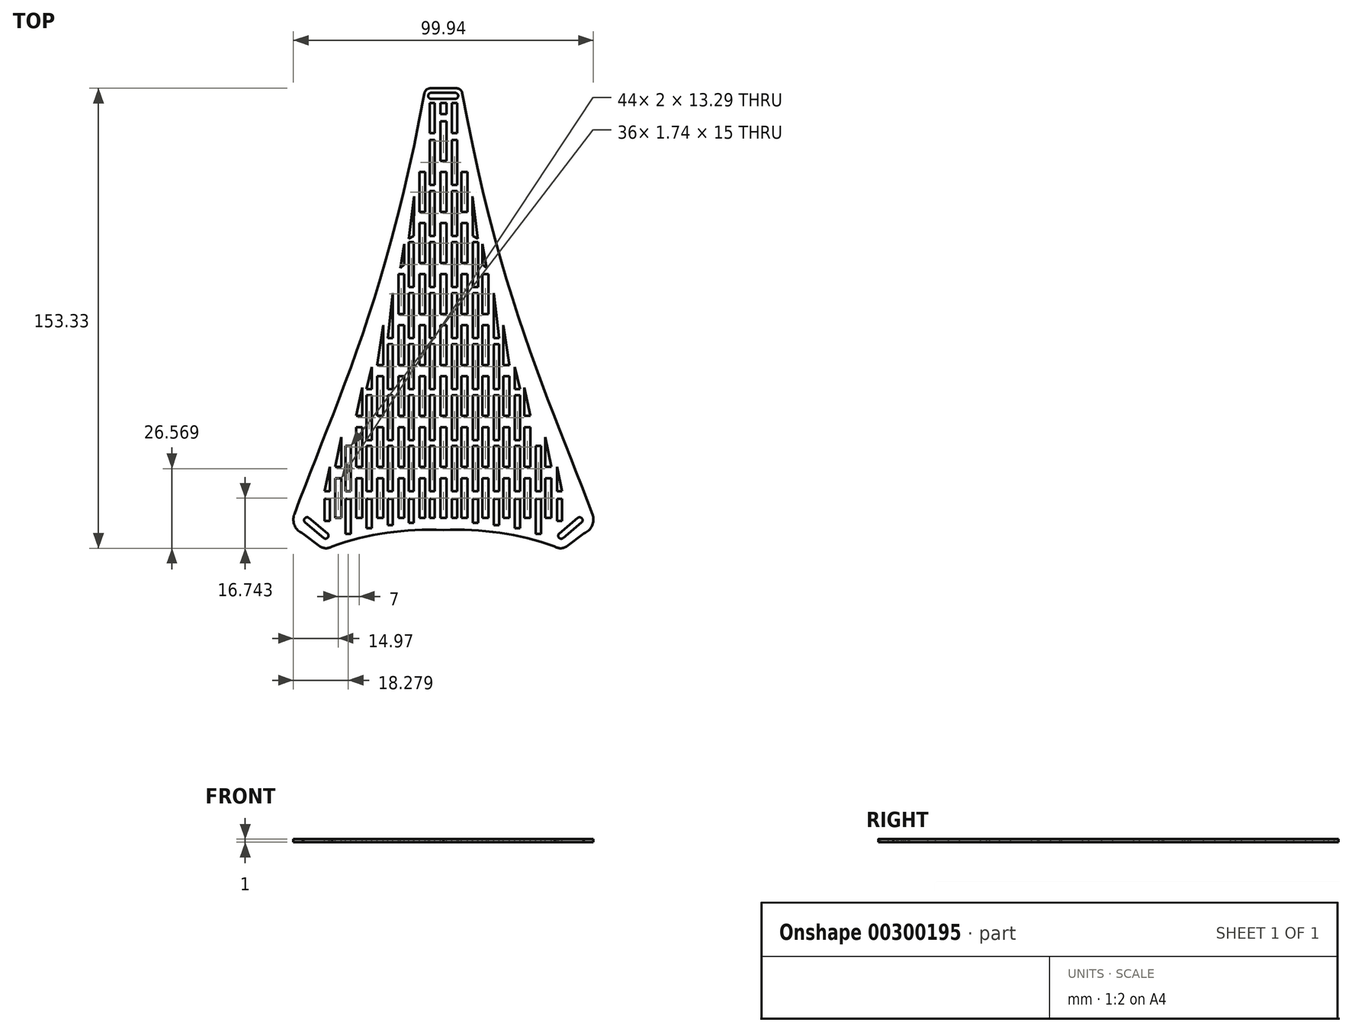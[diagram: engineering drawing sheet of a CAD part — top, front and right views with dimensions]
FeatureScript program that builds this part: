
annotation { "Feature Type Name" : "Feature", "Feature Type Description" : "" }
export const myFeature = defineFeature(function(context is Context, id is Id, definition is map)
    precondition{}
    {
        {
            var Q0;
            Q0=qCreatedBy(makeId("Top.planeOp"),FACE);
            var sketch = newSketch(context, id + "F0", { "sketchPlane" : qUnion([Q0])});
            skFitSpline(sketch, "E0", {"points": [v(-6, 109.23) * mm, v(-51.73, -38.5) * mm], "startDerivative": vector(-41.27, -226.26) * mm, "endDerivative": vector(-40.91, -115.5) * mm});
            skLineSegment(sketch, "E1", {"start": v(-4.34, 109.23) * mm, "end": v(0, 109.23) * mm});
            skArc(sketch, "E2.filletArc", {"start": v(-4.34, 109.23) * mm, "mid": v(-5.62, 108.76) * mm, "end": v(-6.3, 107.6) * mm});
            skArc(sketch, "E3.filletArc", {"start": v(-49.66, -32.79) * mm, "mid": v(-49.54, -36.57) * mm, "end": v(-46.8, -39.17) * mm});
            skLineSegment(sketch, "E4.bottom", {"start": v(-44.75, -34) * mm, "end": v(-38.62, -39.14) * mm});
            skLineSegment(sketch, "E4.top", {"start": v(-46.03, -35.53) * mm, "end": v(-39.9, -40.68) * mm});
            skLineSegment(sketch, "E4.left", {"start": v(-46.16, -34.13) * mm, "end": v(-46.16, -34.13) * mm});
            skLineSegment(sketch, "E4.right", {"start": v(-38.5, -40.55) * mm, "end": v(-38.5, -40.55) * mm});
            skPoint(sketch, "E5.visualSharp", {"position": v(-45.51, -33.36) * mm});
            skArc(sketch, "E5.filletArc", {"start": v(-44.75, -34) * mm, "mid": v(-45.48, -33.77) * mm, "end": v(-46.16, -34.13) * mm});
            skPoint(sketch, "E6.visualSharp", {"position": v(-46.8, -34.9) * mm});
            skArc(sketch, "E6.filletArc", {"start": v(-46.16, -34.13) * mm, "mid": v(-46.39, -34.86) * mm, "end": v(-46.03, -35.53) * mm});
            skPoint(sketch, "E7.visualSharp", {"position": v(-39.14, -41.32) * mm});
            skArc(sketch, "E7.filletArc", {"start": v(-39.9, -40.68) * mm, "mid": v(-39.17, -40.9) * mm, "end": v(-38.5, -40.55) * mm});
            skPoint(sketch, "E8.visualSharp", {"position": v(-37.85, -39.79) * mm});
            skArc(sketch, "E8.filletArc", {"start": v(-38.5, -40.55) * mm, "mid": v(-38.27, -39.82) * mm, "end": v(-38.62, -39.14) * mm});
            skLineSegment(sketch, "E9.bottom", {"start": v(-4.06, 107.72) * mm, "end": v(3.94, 107.72) * mm});
            skLineSegment(sketch, "E9.top", {"start": v(-4.06, 105.72) * mm, "end": v(3.94, 105.72) * mm});
            skLineSegment(sketch, "E9.left", {"start": v(-4.76, 104.67) * mm, "end": v(-4.76, 104.67) * mm});
            skLineSegment(sketch, "E9.right", {"start": v(5.24, 104.67) * mm, "end": v(5.24, 104.67) * mm});
            skPoint(sketch, "E10.visualSharp", {"position": v(-5.06, 107.18) * mm});
            skArc(sketch, "E10.filletArc", {"start": v(-4.06, 107.72) * mm, "mid": v(-4.77, 107.43) * mm, "end": v(-5.06, 106.72) * mm});
            skPoint(sketch, "E11.visualSharp", {"position": v(-5.06, 105.18) * mm});
            skArc(sketch, "E11.filletArc", {"start": v(-5.06, 106.72) * mm, "mid": v(-4.77, 106.01) * mm, "end": v(-4.06, 105.72) * mm});
            skPoint(sketch, "E12.visualSharp", {"position": v(4.94, 105.18) * mm});
            skArc(sketch, "E12.filletArc", {"start": v(3.94, 105.72) * mm, "mid": v(4.65, 106.01) * mm, "end": v(4.94, 106.72) * mm});
            skPoint(sketch, "E13.visualSharp", {"position": v(4.94, 107.18) * mm});
            skArc(sketch, "E13.filletArc", {"start": v(4.94, 106.72) * mm, "mid": v(4.65, 107.43) * mm, "end": v(3.94, 107.72) * mm});
            skArc(sketch, "E14.MirrorCS", {"start": v(46.16, -34.13) * mm, "mid": v(46.39, -34.86) * mm, "end": v(46.03, -35.53) * mm});
            skArc(sketch, "E15.MirrorCS", {"start": v(44.75, -34) * mm, "mid": v(45.48, -33.77) * mm, "end": v(46.16, -34.13) * mm});
            skArc(sketch, "E16.MirrorCS", {"start": v(39.9, -40.68) * mm, "mid": v(39.17, -40.9) * mm, "end": v(38.5, -40.55) * mm});
            skArc(sketch, "E17.MirrorCS", {"start": v(38.5, -40.55) * mm, "mid": v(38.27, -39.82) * mm, "end": v(38.62, -39.14) * mm});
            skLineSegment(sketch, "E18.MirrorCS", {"start": v(38.5, -40.55) * mm, "end": v(38.5, -40.55) * mm});
            skLineSegment(sketch, "E19.MirrorCS", {"start": v(46.16, -34.13) * mm, "end": v(46.16, -34.13) * mm});
            skPoint(sketch, "E20.MirrorP", {"position": v(37.85, -39.79) * mm});
            skLineSegment(sketch, "E21.MirrorCS", {"start": v(44.75, -34) * mm, "end": v(38.62, -39.14) * mm});
            skLineSegment(sketch, "E22.MirrorCS", {"start": v(46.03, -35.53) * mm, "end": v(39.9, -40.68) * mm});
            skPoint(sketch, "E23.MirrorP", {"position": v(45.51, -33.36) * mm});
            skLineSegment(sketch, "E24", {"start": v(-46.8, -39.17) * mm, "end": v(-41.07, -43.44) * mm});
            skArc(sketch, "E25", {"start": v(-41.07, -43.44) * mm, "mid": v(-39.08, -44.1) * mm, "end": v(-37.08, -43.44) * mm});
            skArc(sketch, "E26", {"start": v(0, -38.07) * mm, "mid": v(-18.8, -38.94) * mm, "end": v(-37.08, -43.44) * mm});
            skArc(sketch, "E27.MirrorCS", {"start": v(0, -38.07) * mm, "mid": v(18.8, -38.94) * mm, "end": v(37.08, -43.44) * mm});
            skArc(sketch, "E28.MirrorCS", {"start": v(41.07, -43.44) * mm, "mid": v(39.08, -44.1) * mm, "end": v(37.08, -43.44) * mm});
            skLineSegment(sketch, "E29.MirrorCS", {"start": v(46.8, -39.17) * mm, "end": v(41.07, -43.44) * mm});
            skArc(sketch, "E30.MirrorCS", {"start": v(49.66, -32.79) * mm, "mid": v(49.54, -36.57) * mm, "end": v(46.8, -39.17) * mm});
            skFitSpline(sketch, "E31.MirrorCS", {"points": [v(6, 109.23) * mm, v(51.73, -38.5) * mm], "startDerivative": vector(41.27, -226.26) * mm, "endDerivative": vector(40.91, -115.5) * mm});
            skLineSegment(sketch, "E32.MirrorCS", {"start": v(4.34, 109.23) * mm, "end": v(0, 109.23) * mm});
            skArc(sketch, "E33.MirrorCS", {"start": v(4.34, 109.23) * mm, "mid": v(5.62, 108.76) * mm, "end": v(6.3, 107.6) * mm});
            skSolve(sketch);
        }
        {
            var Q0;
            Q0 = qSketchRegion(id + "F0", true);
            extrude(context, id + "F1", {"entities" : qUnion([Q0]), "depth" : 1 * mm});
        }
        {
            var Q0;
            Q0=makeQuery(id+"F1.opExtrude","CAP_FACE",FACE,{"disambiguationData":[OSD([sQuery(id+"F0.wireOp",EDGE,"5392caef-65bd-4391-aee4-0a75be96cd19"),sQuery(id+"F0.wireOp",EDGE,"2f23e873-a788-427f-9ff4-69841abe22a9"),sQuery(id+"F0.wireOp",EDGE,"E0"),sQuery(id+"F0.wireOp",EDGE,"95mmlAZk-7Ptr-qu52-5vZK-5cVm16xiViI8"),sQuery(id+"F0.wireOp",EDGE,"E1"),sQuery(id+"F0.wireOp",EDGE,"E2.filletArc"),sQuery(id+"F0.wireOp",EDGE,"E3.filletArc"),sQuery(id+"F0.wireOp",EDGE,"6cbc5803-5533-49d3-baa4-ec0fd478d9b7.filletArc"),sQuery(id+"F0.wireOp",EDGE,"bbb3b62d-f833-4483-a488-0af6742b2d680.MirrorCS"),sQuery(id+"F0.wireOp",EDGE,"bbb3b62d-f833-4483-a488-0af6742b2d681.MirrorCS"),sQuery(id+"F0.wireOp",EDGE,"bbb3b62d-f833-4483-a488-0af6742b2d682.MirrorCS"),sQuery(id+"F0.wireOp",EDGE,"bbb3b62d-f833-4483-a488-0af6742b2d683.MirrorCS"),sQuery(id+"F0.wireOp",EDGE,"bbb3b62d-f833-4483-a488-0af6742b2d684.MirrorCS"),sQuery(id+"F0.wireOp",EDGE,"bbb3b62d-f833-4483-a488-0af6742b2d685.MirrorCS"),sQuery(id+"F0.wireOp",EDGE,"bbb3b62d-f833-4483-a488-0af6742b2d687.MirrorCS"),sQuery(id+"F0.wireOp",EDGE,"bbb3b62d-f833-4483-a488-0af6742b2d689.MirrorCS"),sQuery(id+"F0.wireOp",EDGE,"E4.bottom"),sQuery(id+"F0.wireOp",EDGE,"E4.top"),sQuery(id+"F0.wireOp",EDGE,"E5.filletArc"),sQuery(id+"F0.wireOp",EDGE,"E6.filletArc"),sQuery(id+"F0.wireOp",EDGE,"E7.filletArc"),sQuery(id+"F0.wireOp",EDGE,"E8.filletArc"),sQuery(id+"F0.wireOp",EDGE,"E9.bottom"),sQuery(id+"F0.wireOp",EDGE,"E9.top"),sQuery(id+"F0.wireOp",EDGE,"E10.filletArc"),sQuery(id+"F0.wireOp",EDGE,"E11.filletArc"),sQuery(id+"F0.wireOp",EDGE,"E12.filletArc"),sQuery(id+"F0.wireOp",EDGE,"E13.filletArc"),sQuery(id+"F0.wireOp",EDGE,"E14.MirrorCS"),sQuery(id+"F0.wireOp",EDGE,"E15.MirrorCS"),sQuery(id+"F0.wireOp",EDGE,"E16.MirrorCS"),sQuery(id+"F0.wireOp",EDGE,"E17.MirrorCS"),sQuery(id+"F0.wireOp",EDGE,"E21.MirrorCS"),sQuery(id+"F0.wireOp",EDGE,"E22.MirrorCS")])],"isStart":false});
            var sketch = newSketch(context, id + "F2", { "sketchPlane" : qUnion([Q0])});
            skLineSegment(sketch, "E34.bottom", {"start": v(-1, -34) * mm, "end": v(1, -34) * mm});
            skLineSegment(sketch, "E34.top", {"start": v(-1, -20.71) * mm, "end": v(1, -20.71) * mm});
            skLineSegment(sketch, "E34.left", {"start": v(-1, -34) * mm, "end": v(-1, -20.71) * mm});
            skLineSegment(sketch, "E34.right", {"start": v(1, -34) * mm, "end": v(1, -20.71) * mm});
            skPoint(sketch, "E34.middle", {"position": v(0, -27.36) * mm});
            skLineSegment(sketch, "E35.bottom", {"start": v(2.82, -25.03) * mm, "end": v(4.56, -25.03) * mm});
            skLineSegment(sketch, "E35.top", {"start": v(2.82, -10.03) * mm, "end": v(4.56, -10.03) * mm});
            skLineSegment(sketch, "E35.left", {"start": v(2.82, -25.03) * mm, "end": v(2.82, -10.03) * mm});
            skLineSegment(sketch, "E35.right", {"start": v(4.56, -25.03) * mm, "end": v(4.56, -10.03) * mm});
            skPoint(sketch, "E35.middle", {"position": v(3.7, -17.53) * mm});
            skPoint(sketch, "E36.0.1.0", {"position": v(0, -10.36) * mm});
            skLineSegment(sketch, "E36.0.1.1", {"start": v(-1, -17) * mm, "end": v(1, -17) * mm});
            skLineSegment(sketch, "E36.0.1.2", {"start": v(-1, -3.71) * mm, "end": v(1, -3.71) * mm});
            skLineSegment(sketch, "E36.0.1.3", {"start": v(-1, -17) * mm, "end": v(-1, -3.71) * mm});
            skLineSegment(sketch, "E36.0.1.4", {"start": v(1, -17) * mm, "end": v(1, -3.71) * mm});
            skLineSegment(sketch, "E36.0.1.5", {"start": v(2.82, -8.03) * mm, "end": v(4.56, -8.03) * mm});
            skLineSegment(sketch, "E36.0.1.6", {"start": v(2.82, 6.97) * mm, "end": v(4.56, 6.97) * mm});
            skLineSegment(sketch, "E36.0.1.7", {"start": v(2.82, -8.03) * mm, "end": v(2.82, 6.97) * mm});
            skPoint(sketch, "E36.0.1.8", {"position": v(3.7, -0.53) * mm});
            skLineSegment(sketch, "E36.0.1.9", {"start": v(4.56, -8.03) * mm, "end": v(4.56, 6.97) * mm});
            skPoint(sketch, "E36.0.2.0", {"position": v(0, 6.64) * mm});
            skLineSegment(sketch, "E36.0.2.1", {"start": v(-1, 0) * mm, "end": v(1, 0) * mm});
            skLineSegment(sketch, "E36.0.2.2", {"start": v(-1, 13.29) * mm, "end": v(1, 13.29) * mm});
            skLineSegment(sketch, "E36.0.2.3", {"start": v(-1, 0) * mm, "end": v(-1, 13.29) * mm});
            skLineSegment(sketch, "E36.0.2.4", {"start": v(1, 0) * mm, "end": v(1, 13.29) * mm});
            skLineSegment(sketch, "E36.0.2.5", {"start": v(2.82, 8.97) * mm, "end": v(4.56, 8.97) * mm});
            skLineSegment(sketch, "E36.0.2.6", {"start": v(2.82, 23.97) * mm, "end": v(4.56, 23.97) * mm});
            skLineSegment(sketch, "E36.0.2.7", {"start": v(2.82, 8.97) * mm, "end": v(2.82, 23.97) * mm});
            skPoint(sketch, "E36.0.2.8", {"position": v(3.7, 16.47) * mm});
            skLineSegment(sketch, "E36.0.2.9", {"start": v(4.56, 8.97) * mm, "end": v(4.56, 23.97) * mm});
            skPoint(sketch, "E36.0.3.0", {"position": v(0, 23.64) * mm});
            skLineSegment(sketch, "E36.0.3.1", {"start": v(-1, 17) * mm, "end": v(1, 17) * mm});
            skLineSegment(sketch, "E36.0.3.2", {"start": v(-1, 30.29) * mm, "end": v(1, 30.29) * mm});
            skLineSegment(sketch, "E36.0.3.3", {"start": v(-1, 17) * mm, "end": v(-1, 30.29) * mm});
            skLineSegment(sketch, "E36.0.3.4", {"start": v(1, 17) * mm, "end": v(1, 30.29) * mm});
            skLineSegment(sketch, "E36.0.3.5", {"start": v(2.82, 25.97) * mm, "end": v(4.56, 25.97) * mm});
            skLineSegment(sketch, "E36.0.3.6", {"start": v(2.82, 40.97) * mm, "end": v(4.56, 40.97) * mm});
            skLineSegment(sketch, "E36.0.3.7", {"start": v(2.82, 25.97) * mm, "end": v(2.82, 40.97) * mm});
            skPoint(sketch, "E36.0.3.8", {"position": v(3.7, 33.47) * mm});
            skLineSegment(sketch, "E36.0.3.9", {"start": v(4.56, 25.97) * mm, "end": v(4.56, 40.97) * mm});
            skPoint(sketch, "E36.0.4.0", {"position": v(0, 40.64) * mm});
            skLineSegment(sketch, "E36.0.4.1", {"start": v(-1, 34) * mm, "end": v(1, 34) * mm});
            skLineSegment(sketch, "E36.0.4.2", {"start": v(-1, 47.29) * mm, "end": v(1, 47.29) * mm});
            skLineSegment(sketch, "E36.0.4.3", {"start": v(-1, 34) * mm, "end": v(-1, 47.29) * mm});
            skLineSegment(sketch, "E36.0.4.4", {"start": v(1, 34) * mm, "end": v(1, 47.29) * mm});
            skLineSegment(sketch, "E36.0.4.5", {"start": v(2.82, 42.97) * mm, "end": v(4.56, 42.97) * mm});
            skLineSegment(sketch, "E36.0.4.6", {"start": v(2.82, 57.97) * mm, "end": v(4.56, 57.97) * mm});
            skLineSegment(sketch, "E36.0.4.7", {"start": v(2.82, 42.97) * mm, "end": v(2.82, 57.97) * mm});
            skPoint(sketch, "E36.0.4.8", {"position": v(3.7, 50.47) * mm});
            skLineSegment(sketch, "E36.0.4.9", {"start": v(4.56, 42.97) * mm, "end": v(4.56, 57.97) * mm});
            skPoint(sketch, "E36.0.5.0", {"position": v(0, 57.64) * mm});
            skLineSegment(sketch, "E36.0.5.1", {"start": v(-1, 51) * mm, "end": v(1, 51) * mm});
            skLineSegment(sketch, "E36.0.5.2", {"start": v(-1, 64.29) * mm, "end": v(1, 64.29) * mm});
            skLineSegment(sketch, "E36.0.5.3", {"start": v(-1, 51) * mm, "end": v(-1, 64.29) * mm});
            skLineSegment(sketch, "E36.0.5.4", {"start": v(1, 51) * mm, "end": v(1, 64.29) * mm});
            skLineSegment(sketch, "E36.0.5.5", {"start": v(2.82, 59.97) * mm, "end": v(4.56, 59.97) * mm});
            skLineSegment(sketch, "E36.0.5.6", {"start": v(2.82, 74.97) * mm, "end": v(4.56, 74.97) * mm});
            skLineSegment(sketch, "E36.0.5.7", {"start": v(2.82, 59.97) * mm, "end": v(2.82, 74.97) * mm});
            skPoint(sketch, "E36.0.5.8", {"position": v(3.7, 67.47) * mm});
            skLineSegment(sketch, "E36.0.5.9", {"start": v(4.56, 59.97) * mm, "end": v(4.56, 74.97) * mm});
            skPoint(sketch, "E36.0.6.0", {"position": v(0, 74.64) * mm});
            skLineSegment(sketch, "E36.0.6.1", {"start": v(-1, 68) * mm, "end": v(1, 68) * mm});
            skLineSegment(sketch, "E36.0.6.2", {"start": v(-1, 81.29) * mm, "end": v(1, 81.29) * mm});
            skLineSegment(sketch, "E36.0.6.3", {"start": v(-1, 68) * mm, "end": v(-1, 81.29) * mm});
            skLineSegment(sketch, "E36.0.6.4", {"start": v(1, 68) * mm, "end": v(1, 81.29) * mm});
            skLineSegment(sketch, "E36.0.6.5", {"start": v(2.82, 76.97) * mm, "end": v(4.56, 76.97) * mm});
            skLineSegment(sketch, "E36.0.6.6", {"start": v(2.82, 91.97) * mm, "end": v(4.56, 91.97) * mm});
            skLineSegment(sketch, "E36.0.6.7", {"start": v(2.82, 76.97) * mm, "end": v(2.82, 91.97) * mm});
            skPoint(sketch, "E36.0.6.8", {"position": v(3.7, 84.47) * mm});
            skLineSegment(sketch, "E36.0.6.9", {"start": v(4.56, 76.97) * mm, "end": v(4.56, 91.97) * mm});
            skPoint(sketch, "E36.0.7.0", {"position": v(0, 91.64) * mm});
            skLineSegment(sketch, "E36.0.7.1", {"start": v(-1, 85) * mm, "end": v(1, 85) * mm});
            skLineSegment(sketch, "E36.0.7.2", {"start": v(-1, 98.29) * mm, "end": v(1, 98.29) * mm});
            skLineSegment(sketch, "E36.0.7.3", {"start": v(-1, 85) * mm, "end": v(-1, 98.29) * mm});
            skLineSegment(sketch, "E36.0.7.4", {"start": v(1, 85) * mm, "end": v(1, 98.29) * mm});
            skPoint(sketch, "E36.1.0.0", {"position": v(7, -27.36) * mm});
            skLineSegment(sketch, "E36.1.0.1", {"start": v(6, -34) * mm, "end": v(8, -34) * mm});
            skLineSegment(sketch, "E36.1.0.2", {"start": v(6, -20.71) * mm, "end": v(8, -20.71) * mm});
            skLineSegment(sketch, "E36.1.0.3", {"start": v(6, -34) * mm, "end": v(6, -20.71) * mm});
            skLineSegment(sketch, "E36.1.0.4", {"start": v(8, -34) * mm, "end": v(8, -20.71) * mm});
            skLineSegment(sketch, "E36.1.0.5", {"start": v(9.82, -25.03) * mm, "end": v(11.56, -25.03) * mm});
            skLineSegment(sketch, "E36.1.0.6", {"start": v(9.82, -10.03) * mm, "end": v(11.56, -10.03) * mm});
            skLineSegment(sketch, "E36.1.0.7", {"start": v(9.82, -25.03) * mm, "end": v(9.82, -10.03) * mm});
            skPoint(sketch, "E36.1.0.8", {"position": v(10.7, -17.53) * mm});
            skLineSegment(sketch, "E36.1.0.9", {"start": v(11.56, -25.03) * mm, "end": v(11.56, -10.03) * mm});
            skPoint(sketch, "E36.1.1.0", {"position": v(7, -10.36) * mm});
            skLineSegment(sketch, "E36.1.1.1", {"start": v(6, -17) * mm, "end": v(8, -17) * mm});
            skLineSegment(sketch, "E36.1.1.2", {"start": v(6, -3.71) * mm, "end": v(8, -3.71) * mm});
            skLineSegment(sketch, "E36.1.1.3", {"start": v(6, -17) * mm, "end": v(6, -3.71) * mm});
            skLineSegment(sketch, "E36.1.1.4", {"start": v(8, -17) * mm, "end": v(8, -3.71) * mm});
            skLineSegment(sketch, "E36.1.1.5", {"start": v(9.82, -8.03) * mm, "end": v(11.56, -8.03) * mm});
            skLineSegment(sketch, "E36.1.1.6", {"start": v(9.82, 6.97) * mm, "end": v(11.56, 6.97) * mm});
            skLineSegment(sketch, "E36.1.1.7", {"start": v(9.82, -8.03) * mm, "end": v(9.82, 6.97) * mm});
            skPoint(sketch, "E36.1.1.8", {"position": v(10.7, -0.53) * mm});
            skLineSegment(sketch, "E36.1.1.9", {"start": v(11.56, -8.03) * mm, "end": v(11.56, 6.97) * mm});
            skPoint(sketch, "E36.1.2.0", {"position": v(7, 6.64) * mm});
            skLineSegment(sketch, "E36.1.2.1", {"start": v(6, 0) * mm, "end": v(8, 0) * mm});
            skLineSegment(sketch, "E36.1.2.2", {"start": v(6, 13.29) * mm, "end": v(8, 13.29) * mm});
            skLineSegment(sketch, "E36.1.2.3", {"start": v(6, 0) * mm, "end": v(6, 13.29) * mm});
            skLineSegment(sketch, "E36.1.2.4", {"start": v(8, 0) * mm, "end": v(8, 13.29) * mm});
            skLineSegment(sketch, "E36.1.2.5", {"start": v(9.82, 8.97) * mm, "end": v(11.56, 8.97) * mm});
            skLineSegment(sketch, "E36.1.2.6", {"start": v(9.82, 23.97) * mm, "end": v(11.56, 23.97) * mm});
            skLineSegment(sketch, "E36.1.2.7", {"start": v(9.82, 8.97) * mm, "end": v(9.82, 23.97) * mm});
            skPoint(sketch, "E36.1.2.8", {"position": v(10.7, 16.47) * mm});
            skLineSegment(sketch, "E36.1.2.9", {"start": v(11.56, 8.97) * mm, "end": v(11.56, 23.97) * mm});
            skPoint(sketch, "E36.1.3.0", {"position": v(7, 23.64) * mm});
            skLineSegment(sketch, "E36.1.3.1", {"start": v(6, 17) * mm, "end": v(8, 17) * mm});
            skLineSegment(sketch, "E36.1.3.2", {"start": v(6, 30.29) * mm, "end": v(8, 30.29) * mm});
            skLineSegment(sketch, "E36.1.3.3", {"start": v(6, 17) * mm, "end": v(6, 30.29) * mm});
            skLineSegment(sketch, "E36.1.3.4", {"start": v(8, 17) * mm, "end": v(8, 30.29) * mm});
            skLineSegment(sketch, "E36.1.3.5", {"start": v(9.82, 25.97) * mm, "end": v(11.56, 25.97) * mm});
            skLineSegment(sketch, "E36.1.3.6", {"start": v(9.82, 40.97) * mm, "end": v(11.56, 40.97) * mm});
            skLineSegment(sketch, "E36.1.3.7", {"start": v(9.82, 25.97) * mm, "end": v(9.82, 40.97) * mm});
            skPoint(sketch, "E36.1.3.8", {"position": v(10.7, 33.47) * mm});
            skLineSegment(sketch, "E36.1.3.9", {"start": v(11.56, 25.97) * mm, "end": v(11.56, 40.97) * mm});
            skPoint(sketch, "E36.1.4.0", {"position": v(7, 40.64) * mm});
            skLineSegment(sketch, "E36.1.4.1", {"start": v(6, 34) * mm, "end": v(8, 34) * mm});
            skLineSegment(sketch, "E36.1.4.2", {"start": v(6, 47.29) * mm, "end": v(8, 47.29) * mm});
            skLineSegment(sketch, "E36.1.4.3", {"start": v(6, 34) * mm, "end": v(6, 47.29) * mm});
            skLineSegment(sketch, "E36.1.4.4", {"start": v(8, 34) * mm, "end": v(8, 47.29) * mm});
            skLineSegment(sketch, "E36.1.4.5", {"start": v(9.82, 42.97) * mm, "end": v(11.56, 42.97) * mm});
            skLineSegment(sketch, "E36.1.4.6", {"start": v(9.82, 57.97) * mm, "end": v(11.56, 57.97) * mm});
            skLineSegment(sketch, "E36.1.4.7", {"start": v(9.82, 42.97) * mm, "end": v(9.82, 57.97) * mm});
            skPoint(sketch, "E36.1.4.8", {"position": v(10.7, 50.47) * mm});
            skLineSegment(sketch, "E36.1.4.9", {"start": v(11.56, 42.97) * mm, "end": v(11.56, 57.97) * mm});
            skPoint(sketch, "E36.1.5.0", {"position": v(7, 57.64) * mm});
            skLineSegment(sketch, "E36.1.5.1", {"start": v(6, 51) * mm, "end": v(8, 51) * mm});
            skLineSegment(sketch, "E36.1.5.2", {"start": v(6, 64.29) * mm, "end": v(8, 64.29) * mm});
            skLineSegment(sketch, "E36.1.5.3", {"start": v(6, 51) * mm, "end": v(6, 64.29) * mm});
            skLineSegment(sketch, "E36.1.5.4", {"start": v(8, 51) * mm, "end": v(8, 64.29) * mm});
            skPoint(sketch, "E36.1.6.0", {"position": v(7, 74.64) * mm});
            skLineSegment(sketch, "E36.1.6.1", {"start": v(6, 68) * mm, "end": v(8, 68) * mm});
            skLineSegment(sketch, "E36.1.6.2", {"start": v(6, 81.29) * mm, "end": v(8, 81.29) * mm});
            skLineSegment(sketch, "E36.1.6.3", {"start": v(6, 68) * mm, "end": v(6, 81.29) * mm});
            skLineSegment(sketch, "E36.1.6.4", {"start": v(8, 68) * mm, "end": v(8, 81.29) * mm});
            skPoint(sketch, "E36.2.0.0", {"position": v(14, -27.36) * mm});
            skLineSegment(sketch, "E36.2.0.1", {"start": v(13, -34) * mm, "end": v(15, -34) * mm});
            skLineSegment(sketch, "E36.2.0.2", {"start": v(13, -20.71) * mm, "end": v(15, -20.71) * mm});
            skLineSegment(sketch, "E36.2.0.3", {"start": v(13, -34) * mm, "end": v(13, -20.71) * mm});
            skLineSegment(sketch, "E36.2.0.4", {"start": v(15, -34) * mm, "end": v(15, -20.71) * mm});
            skLineSegment(sketch, "E36.2.0.5", {"start": v(16.82, -25.03) * mm, "end": v(18.56, -25.03) * mm});
            skLineSegment(sketch, "E36.2.0.6", {"start": v(16.82, -10.03) * mm, "end": v(18.56, -10.03) * mm});
            skLineSegment(sketch, "E36.2.0.7", {"start": v(16.82, -25.03) * mm, "end": v(16.82, -10.03) * mm});
            skPoint(sketch, "E36.2.0.8", {"position": v(17.7, -17.53) * mm});
            skLineSegment(sketch, "E36.2.0.9", {"start": v(18.56, -25.03) * mm, "end": v(18.56, -10.03) * mm});
            skPoint(sketch, "E36.2.1.0", {"position": v(14, -10.36) * mm});
            skLineSegment(sketch, "E36.2.1.1", {"start": v(13, -17) * mm, "end": v(15, -17) * mm});
            skLineSegment(sketch, "E36.2.1.2", {"start": v(13, -3.71) * mm, "end": v(15, -3.71) * mm});
            skLineSegment(sketch, "E36.2.1.3", {"start": v(13, -17) * mm, "end": v(13, -3.71) * mm});
            skLineSegment(sketch, "E36.2.1.4", {"start": v(15, -17) * mm, "end": v(15, -3.71) * mm});
            skLineSegment(sketch, "E36.2.1.5", {"start": v(16.82, -8.03) * mm, "end": v(18.56, -8.03) * mm});
            skLineSegment(sketch, "E36.2.1.6", {"start": v(16.82, 6.97) * mm, "end": v(18.56, 6.97) * mm});
            skLineSegment(sketch, "E36.2.1.7", {"start": v(16.82, -8.03) * mm, "end": v(16.82, 6.97) * mm});
            skPoint(sketch, "E36.2.1.8", {"position": v(17.7, -0.53) * mm});
            skLineSegment(sketch, "E36.2.1.9", {"start": v(18.56, -8.03) * mm, "end": v(18.56, 6.97) * mm});
            skPoint(sketch, "E36.2.2.0", {"position": v(14, 6.64) * mm});
            skLineSegment(sketch, "E36.2.2.1", {"start": v(13, 0) * mm, "end": v(15, 0) * mm});
            skLineSegment(sketch, "E36.2.2.2", {"start": v(13, 13.29) * mm, "end": v(15, 13.29) * mm});
            skLineSegment(sketch, "E36.2.2.3", {"start": v(13, 0) * mm, "end": v(13, 13.29) * mm});
            skLineSegment(sketch, "E36.2.2.4", {"start": v(15, 0) * mm, "end": v(15, 13.29) * mm});
            skLineSegment(sketch, "E36.2.2.5", {"start": v(16.82, 8.97) * mm, "end": v(18.56, 8.97) * mm});
            skLineSegment(sketch, "E36.2.2.6", {"start": v(16.82, 23.97) * mm, "end": v(18.56, 23.97) * mm});
            skLineSegment(sketch, "E36.2.2.7", {"start": v(16.82, 8.97) * mm, "end": v(16.82, 23.97) * mm});
            skPoint(sketch, "E36.2.2.8", {"position": v(17.7, 16.47) * mm});
            skLineSegment(sketch, "E36.2.2.9", {"start": v(18.56, 8.97) * mm, "end": v(18.56, 23.97) * mm});
            skPoint(sketch, "E36.2.3.0", {"position": v(14, 23.64) * mm});
            skLineSegment(sketch, "E36.2.3.1", {"start": v(13, 17) * mm, "end": v(15, 17) * mm});
            skLineSegment(sketch, "E36.2.3.2", {"start": v(13, 30.29) * mm, "end": v(15, 30.29) * mm});
            skLineSegment(sketch, "E36.2.3.3", {"start": v(13, 17) * mm, "end": v(13, 30.29) * mm});
            skLineSegment(sketch, "E36.2.3.4", {"start": v(15, 17) * mm, "end": v(15, 30.29) * mm});
            skLineSegment(sketch, "E36.2.3.5", {"start": v(16.82, 25.97) * mm, "end": v(18.56, 25.97) * mm});
            skLineSegment(sketch, "E36.2.3.7", {"start": v(16.82, 25.97) * mm, "end": v(16.82, 40.97) * mm});
            skPoint(sketch, "E36.2.3.8", {"position": v(17.7, 33.47) * mm});
            skPoint(sketch, "E36.2.4.0", {"position": v(14, 40.64) * mm});
            skLineSegment(sketch, "E36.2.4.1", {"start": v(13, 34) * mm, "end": v(15, 34) * mm});
            skLineSegment(sketch, "E36.2.4.2", {"start": v(13, 47.29) * mm, "end": v(15, 47.29) * mm});
            skLineSegment(sketch, "E36.2.4.3", {"start": v(13, 34) * mm, "end": v(13, 47.29) * mm});
            skLineSegment(sketch, "E36.2.4.4", {"start": v(15, 34) * mm, "end": v(15, 47.29) * mm});
            skPoint(sketch, "E36.3.0.0", {"position": v(21, -27.36) * mm});
            skLineSegment(sketch, "E36.3.0.1", {"start": v(20, -34) * mm, "end": v(22, -34) * mm});
            skLineSegment(sketch, "E36.3.0.2", {"start": v(20, -20.71) * mm, "end": v(22, -20.71) * mm});
            skLineSegment(sketch, "E36.3.0.3", {"start": v(20, -34) * mm, "end": v(20, -20.71) * mm});
            skLineSegment(sketch, "E36.3.0.4", {"start": v(22, -34) * mm, "end": v(22, -20.71) * mm});
            skLineSegment(sketch, "E36.3.0.5", {"start": v(23.82, -25.03) * mm, "end": v(25.56, -25.03) * mm});
            skLineSegment(sketch, "E36.3.0.6", {"start": v(23.82, -10.03) * mm, "end": v(25.56, -10.03) * mm});
            skLineSegment(sketch, "E36.3.0.7", {"start": v(23.82, -25.03) * mm, "end": v(23.82, -10.03) * mm});
            skPoint(sketch, "E36.3.0.8", {"position": v(24.7, -17.53) * mm});
            skLineSegment(sketch, "E36.3.0.9", {"start": v(25.56, -25.03) * mm, "end": v(25.56, -10.03) * mm});
            skPoint(sketch, "E36.3.1.0", {"position": v(21, -10.36) * mm});
            skLineSegment(sketch, "E36.3.1.1", {"start": v(20, -17) * mm, "end": v(22, -17) * mm});
            skLineSegment(sketch, "E36.3.1.2", {"start": v(20, -3.71) * mm, "end": v(22, -3.71) * mm});
            skLineSegment(sketch, "E36.3.1.3", {"start": v(20, -17) * mm, "end": v(20, -3.71) * mm});
            skLineSegment(sketch, "E36.3.1.4", {"start": v(22, -17) * mm, "end": v(22, -3.71) * mm});
            skLineSegment(sketch, "E36.3.1.5", {"start": v(23.82, -8.03) * mm, "end": v(25.56, -8.03) * mm});
            skLineSegment(sketch, "E36.3.1.6", {"start": v(23.82, 6.97) * mm, "end": v(25.56, 6.97) * mm});
            skLineSegment(sketch, "E36.3.1.7", {"start": v(23.82, -8.03) * mm, "end": v(23.82, 6.97) * mm});
            skPoint(sketch, "E36.3.1.8", {"position": v(24.7, -0.53) * mm});
            skLineSegment(sketch, "E36.3.1.9", {"start": v(25.56, -8.03) * mm, "end": v(25.56, 6.97) * mm});
            skPoint(sketch, "E36.3.2.0", {"position": v(21, 6.64) * mm});
            skLineSegment(sketch, "E36.3.2.1", {"start": v(20, 0) * mm, "end": v(22, 0) * mm});
            skLineSegment(sketch, "E36.3.2.2", {"start": v(20, 13.29) * mm, "end": v(22, 13.29) * mm});
            skLineSegment(sketch, "E36.3.2.3", {"start": v(20, 0) * mm, "end": v(20, 13.29) * mm});
            skLineSegment(sketch, "E36.3.2.4", {"start": v(22, 0) * mm, "end": v(22, 13.29) * mm});
            skLineSegment(sketch, "E36.3.2.5", {"start": v(23.82, 8.97) * mm, "end": v(25.56, 8.97) * mm});
            skLineSegment(sketch, "E36.3.3.1", {"start": v(20, 17) * mm, "end": v(22, 17) * mm});
            skLineSegment(sketch, "E36.3.3.3", {"start": v(20, 17) * mm, "end": v(20, 30.29) * mm});
            skPoint(sketch, "E36.4.0.0", {"position": v(28, -27.36) * mm});
            skLineSegment(sketch, "E36.4.0.1", {"start": v(27, -34) * mm, "end": v(29, -34) * mm});
            skLineSegment(sketch, "E36.4.0.2", {"start": v(27, -20.71) * mm, "end": v(29, -20.71) * mm});
            skLineSegment(sketch, "E36.4.0.3", {"start": v(27, -34) * mm, "end": v(27, -20.71) * mm});
            skLineSegment(sketch, "E36.4.0.4", {"start": v(29, -34) * mm, "end": v(29, -20.71) * mm});
            skLineSegment(sketch, "E36.4.0.5", {"start": v(30.82, -25.03) * mm, "end": v(32.56, -25.03) * mm});
            skLineSegment(sketch, "E36.4.0.6", {"start": v(30.82, -10.03) * mm, "end": v(32.56, -10.03) * mm});
            skLineSegment(sketch, "E36.4.0.7", {"start": v(30.82, -25.03) * mm, "end": v(30.82, -10.03) * mm});
            skPoint(sketch, "E36.4.0.8", {"position": v(31.7, -17.53) * mm});
            skLineSegment(sketch, "E36.4.0.9", {"start": v(32.56, -25.03) * mm, "end": v(32.56, -10.03) * mm});
            skPoint(sketch, "E36.4.1.0", {"position": v(28, -10.36) * mm});
            skLineSegment(sketch, "E36.4.1.1", {"start": v(27, -17) * mm, "end": v(29, -17) * mm});
            skLineSegment(sketch, "E36.4.1.2", {"start": v(27, -3.71) * mm, "end": v(29, -3.71) * mm});
            skLineSegment(sketch, "E36.4.1.3", {"start": v(27, -17) * mm, "end": v(27, -3.71) * mm});
            skLineSegment(sketch, "E36.4.1.4", {"start": v(29, -17) * mm, "end": v(29, -3.71) * mm});
            skLineSegment(sketch, "E36.4.1.5", {"start": v(30.82, -8.03) * mm, "end": v(32.56, -8.03) * mm});
            skLineSegment(sketch, "E36.4.1.7", {"start": v(30.82, -8.03) * mm, "end": v(30.82, 1.15) * mm});
            skLineSegment(sketch, "E36.4.2.1", {"start": v(27, 0) * mm, "end": v(29, 0) * mm});
            skLineSegment(sketch, "E36.4.2.3", {"start": v(27, 0) * mm, "end": v(27, 9.49) * mm});
            skPoint(sketch, "E36.5.0.0", {"position": v(35, -27.36) * mm});
            skLineSegment(sketch, "E36.5.0.1", {"start": v(34, -34) * mm, "end": v(36, -34) * mm});
            skLineSegment(sketch, "E36.5.0.2", {"start": v(34, -20.71) * mm, "end": v(36, -20.71) * mm});
            skLineSegment(sketch, "E36.5.0.3", {"start": v(34, -34) * mm, "end": v(34, -20.71) * mm});
            skLineSegment(sketch, "E36.5.0.4", {"start": v(36, -34) * mm, "end": v(36, -20.71) * mm});
            skLineSegment(sketch, "E36.5.0.5", {"start": v(37.82, -25.03) * mm, "end": v(39.56, -25.03) * mm});
            skLineSegment(sketch, "E36.5.0.7", {"start": v(37.82, -25.03) * mm, "end": v(37.82, -17) * mm});
            skLineSegment(sketch, "E36.5.1.1", {"start": v(34, -17) * mm, "end": v(36, -17) * mm});
            skLineSegment(sketch, "E36.5.1.3", {"start": v(34, -17) * mm, "end": v(34, -7.06) * mm});
            skLineSegment(sketch, "E36.direction1", {"start": v(-1, -34) * mm, "end": v(6, -34) * mm, "construction": true});
            skLineSegment(sketch, "E36.direction2", {"start": v(-1, -34) * mm, "end": v(-1, -17) * mm, "construction": true});
            skLineSegment(sketch, "E37", {"start": v(16.82, 40.97) * mm, "end": v(18.56, 25.97) * mm});
            skLineSegment(sketch, "E38", {"start": v(20, 30.29) * mm, "end": v(22, 17) * mm});
            skLineSegment(sketch, "E39", {"start": v(23.82, 8.97) * mm, "end": v(23.82, 16.33) * mm});
            skLineSegment(sketch, "E40", {"start": v(23.82, 16.33) * mm, "end": v(25.56, 8.97) * mm});
            skLineSegment(sketch, "E41", {"start": v(27, 9.49) * mm, "end": v(29, 0) * mm});
            skLineSegment(sketch, "E42", {"start": v(30.61, 2.6) * mm, "end": v(32.56, -8.03) * mm});
            skLineSegment(sketch, "E43", {"start": v(34, -7.06) * mm, "end": v(36, -17) * mm});
            skLineSegment(sketch, "E44", {"start": v(37.82, -17) * mm, "end": v(39.56, -25.03) * mm});
            skLineSegment(sketch, "E45.2.3.5", {"start": v(9.82, 59.99) * mm, "end": v(11.5, 59.17) * mm});
            skLineSegment(sketch, "E45.2.3.7", {"start": v(9.82, 59.99) * mm, "end": v(9.72, 73.26) * mm});
            skPoint(sketch, "E45.2.3.8", {"position": v(10.72, 65.76) * mm});
            skLineSegment(sketch, "E46", {"start": v(9.72, 73.26) * mm, "end": v(11.5, 59.17) * mm});
            skLineSegment(sketch, "E47.2.3.5", {"start": v(13, 50.47) * mm, "end": v(14.36, 49.35) * mm});
            skLineSegment(sketch, "E47.2.3.7", {"start": v(13, 50.47) * mm, "end": v(13, 57.3) * mm});
            skPoint(sketch, "E47.2.3.8", {"position": v(14, 56.26) * mm});
            skLineSegment(sketch, "E48", {"start": v(13, 57.3) * mm, "end": v(14.36, 49.35) * mm});
            skLineSegment(sketch, "E49.bottom", {"start": v(2.82, 94.32) * mm, "end": v(4.56, 94.32) * mm});
            skLineSegment(sketch, "E49.top", {"start": v(2.82, 104.34) * mm, "end": v(4.56, 104.34) * mm});
            skLineSegment(sketch, "E49.left", {"start": v(2.82, 94.32) * mm, "end": v(2.82, 104.34) * mm});
            skLineSegment(sketch, "E49.right", {"start": v(4.56, 94.32) * mm, "end": v(4.56, 104.34) * mm});
            skLineSegment(sketch, "E50.bottom", {"start": v(1, 100.63) * mm, "end": v(-1, 100.63) * mm});
            skLineSegment(sketch, "E50.top", {"start": v(1, 104.34) * mm, "end": v(-1, 104.34) * mm});
            skLineSegment(sketch, "E50.left", {"start": v(1, 100.63) * mm, "end": v(1, 104.34) * mm});
            skLineSegment(sketch, "E50.right", {"start": v(-1, 100.63) * mm, "end": v(-1, 104.34) * mm});
            skLineSegment(sketch, "E51.bottom", {"start": v(9.82, -27.6) * mm, "end": v(11.56, -27.6) * mm});
            skLineSegment(sketch, "E51.top", {"start": v(9.82, -35.66) * mm, "end": v(11.56, -35.66) * mm});
            skLineSegment(sketch, "E51.left", {"start": v(9.82, -27.6) * mm, "end": v(9.82, -35.66) * mm});
            skLineSegment(sketch, "E51.right", {"start": v(11.56, -27.6) * mm, "end": v(11.56, -35.66) * mm});
            skLineSegment(sketch, "E52.bottom", {"start": v(4.56, -27.6) * mm, "end": v(2.82, -27.6) * mm});
            skLineSegment(sketch, "E52.top", {"start": v(4.56, -34) * mm, "end": v(2.82, -34) * mm});
            skLineSegment(sketch, "E52.left", {"start": v(4.56, -27.6) * mm, "end": v(4.56, -34) * mm});
            skLineSegment(sketch, "E52.right", {"start": v(2.82, -27.6) * mm, "end": v(2.82, -34) * mm});
            skLineSegment(sketch, "E53.bottom", {"start": v(16.82, -27.6) * mm, "end": v(18.56, -27.6) * mm});
            skLineSegment(sketch, "E53.top", {"start": v(16.82, -36.37) * mm, "end": v(18.56, -36.37) * mm});
            skLineSegment(sketch, "E53.left", {"start": v(16.82, -27.6) * mm, "end": v(16.82, -36.37) * mm});
            skLineSegment(sketch, "E53.right", {"start": v(18.56, -27.6) * mm, "end": v(18.56, -36.37) * mm});
            skLineSegment(sketch, "E54.bottom", {"start": v(23.82, -27.6) * mm, "end": v(25.56, -27.6) * mm});
            skLineSegment(sketch, "E54.top", {"start": v(23.82, -37.43) * mm, "end": v(25.56, -37.43) * mm});
            skLineSegment(sketch, "E54.left", {"start": v(23.82, -27.6) * mm, "end": v(23.82, -37.43) * mm});
            skLineSegment(sketch, "E54.right", {"start": v(25.56, -27.6) * mm, "end": v(25.56, -37.43) * mm});
            skLineSegment(sketch, "E55.bottom", {"start": v(32.56, -27.6) * mm, "end": v(30.82, -27.6) * mm});
            skLineSegment(sketch, "E55.top", {"start": v(32.56, -39.31) * mm, "end": v(30.82, -39.31) * mm});
            skLineSegment(sketch, "E55.left", {"start": v(32.56, -27.6) * mm, "end": v(32.56, -39.31) * mm});
            skLineSegment(sketch, "E55.right", {"start": v(30.82, -27.6) * mm, "end": v(30.82, -39.31) * mm});
            skLineSegment(sketch, "E56.bottom", {"start": v(37.82, -27.6) * mm, "end": v(39.56, -27.6) * mm});
            skLineSegment(sketch, "E56.top", {"start": v(37.82, -35.03) * mm, "end": v(39.56, -35.03) * mm});
            skLineSegment(sketch, "E56.left", {"start": v(37.82, -27.6) * mm, "end": v(37.82, -35.03) * mm});
            skLineSegment(sketch, "E56.right", {"start": v(39.56, -27.6) * mm, "end": v(39.56, -35.03) * mm});
            skLineSegment(sketch, "E57.MirrorCS", {"start": v(-4.56, -34) * mm, "end": v(-2.82, -34) * mm});
            skLineSegment(sketch, "E58.MirrorCS", {"start": v(1, -34) * mm, "end": v(-1, -34) * mm});
            skLineSegment(sketch, "E59.MirrorCS", {"start": v(1, -34) * mm, "end": v(-6, -34) * mm, "construction": true});
            skLineSegment(sketch, "E60.MirrorCS", {"start": v(-16.82, -27.6) * mm, "end": v(-18.56, -27.6) * mm});
            skLineSegment(sketch, "E61.MirrorCS", {"start": v(-13, -20.71) * mm, "end": v(-15, -20.71) * mm});
            skLineSegment(sketch, "E62.MirrorCS", {"start": v(-23.82, -25.03) * mm, "end": v(-25.56, -25.03) * mm});
            skLineSegment(sketch, "E63.MirrorCS", {"start": v(-23.82, 8.97) * mm, "end": v(-25.56, 8.97) * mm});
            skLineSegment(sketch, "E64.MirrorCS", {"start": v(-13, 13.29) * mm, "end": v(-15, 13.29) * mm});
            skLineSegment(sketch, "E65.MirrorCS", {"start": v(-2.82, 74.97) * mm, "end": v(-4.56, 74.97) * mm});
            skLineSegment(sketch, "E66.MirrorCS", {"start": v(-6, -20.71) * mm, "end": v(-8, -20.71) * mm});
            skLineSegment(sketch, "E67.MirrorCS", {"start": v(-9.82, 57.97) * mm, "end": v(-11.56, 57.97) * mm});
            skLineSegment(sketch, "E68.MirrorCS", {"start": v(-6, 0) * mm, "end": v(-8, 0) * mm});
            skLineSegment(sketch, "E69.MirrorCS", {"start": v(-30.82, -10.03) * mm, "end": v(-32.56, -10.03) * mm});
            skLineSegment(sketch, "E70.MirrorCS", {"start": v(-27, -17) * mm, "end": v(-29, -17) * mm});
            skLineSegment(sketch, "E71.MirrorCS", {"start": v(-20, 17) * mm, "end": v(-22, 17) * mm});
            skLineSegment(sketch, "E72.MirrorCS", {"start": v(-23.82, -10.03) * mm, "end": v(-25.56, -10.03) * mm});
            skLineSegment(sketch, "E73.MirrorCS", {"start": v(-6, 13.29) * mm, "end": v(-8, 13.29) * mm});
            skLineSegment(sketch, "E74.MirrorCS", {"start": v(-2.82, -8.03) * mm, "end": v(-4.56, -8.03) * mm});
            skLineSegment(sketch, "E75.MirrorCS", {"start": v(-13, 50.47) * mm, "end": v(-14.36, 49.35) * mm});
            skLineSegment(sketch, "E76.MirrorCS", {"start": v(-2.82, 8.97) * mm, "end": v(-4.56, 8.97) * mm});
            skLineSegment(sketch, "E77.MirrorCS", {"start": v(-2.82, 42.97) * mm, "end": v(-4.56, 42.97) * mm});
            skLineSegment(sketch, "E78.MirrorCS", {"start": v(-6, 51) * mm, "end": v(-8, 51) * mm});
            skLineSegment(sketch, "E79.MirrorCS", {"start": v(-6, 47.29) * mm, "end": v(-8, 47.29) * mm});
            skLineSegment(sketch, "E80.MirrorCS", {"start": v(-6, -17) * mm, "end": v(-8, -17) * mm});
            skLineSegment(sketch, "E81.MirrorCS", {"start": v(-6, 17) * mm, "end": v(-8, 17) * mm});
            skLineSegment(sketch, "E82.MirrorCS", {"start": v(-13, 17) * mm, "end": v(-15, 17) * mm});
            skLineSegment(sketch, "E83.MirrorCS", {"start": v(-13, -17) * mm, "end": v(-15, -17) * mm});
            skLineSegment(sketch, "E84.MirrorCS", {"start": v(-9.82, -10.03) * mm, "end": v(-11.56, -10.03) * mm});
            skLineSegment(sketch, "E85.MirrorCS", {"start": v(-2.82, 40.97) * mm, "end": v(-4.56, 40.97) * mm});
            skLineSegment(sketch, "E86.MirrorCS", {"start": v(-2.82, 57.97) * mm, "end": v(-4.56, 57.97) * mm});
            skLineSegment(sketch, "E87.MirrorCS", {"start": v(-13, 0) * mm, "end": v(-15, 0) * mm});
            skLineSegment(sketch, "E88.MirrorCS", {"start": v(-2.82, 23.97) * mm, "end": v(-4.56, 23.97) * mm});
            skLineSegment(sketch, "E89.MirrorCS", {"start": v(-6, 64.29) * mm, "end": v(-8, 64.29) * mm});
            skLineSegment(sketch, "E90.MirrorCS", {"start": v(-6, 30.29) * mm, "end": v(-8, 30.29) * mm});
            skLineSegment(sketch, "E91.MirrorCS", {"start": v(-6, -3.71) * mm, "end": v(-8, -3.71) * mm});
            skLineSegment(sketch, "E92.MirrorCS", {"start": v(-13, 30.29) * mm, "end": v(-15, 30.29) * mm});
            skLineSegment(sketch, "E93.MirrorCS", {"start": v(-13, -3.71) * mm, "end": v(-15, -3.71) * mm});
            skLineSegment(sketch, "E94.MirrorCS", {"start": v(-9.82, -27.6) * mm, "end": v(-11.56, -27.6) * mm});
            skLineSegment(sketch, "E95.MirrorCS", {"start": v(-32.56, -27.6) * mm, "end": v(-30.82, -27.6) * mm});
            skLineSegment(sketch, "E96.MirrorCS", {"start": v(-13, 34) * mm, "end": v(-15, 34) * mm});
            skLineSegment(sketch, "E97.MirrorCS", {"start": v(-27, -20.71) * mm, "end": v(-29, -20.71) * mm});
            skLineSegment(sketch, "E98.MirrorCS", {"start": v(-20, -17) * mm, "end": v(-22, -17) * mm});
            skLineSegment(sketch, "E99.MirrorCS", {"start": v(-34, -20.71) * mm, "end": v(-36, -20.71) * mm});
            skLineSegment(sketch, "E100.MirrorCS", {"start": v(-20, 13.29) * mm, "end": v(-22, 13.29) * mm});
            skLineSegment(sketch, "E101.MirrorCS", {"start": v(-27, -3.71) * mm, "end": v(-29, -3.71) * mm});
            skLineSegment(sketch, "E102.MirrorCS", {"start": v(-34, -17) * mm, "end": v(-36, -17) * mm});
            skLineSegment(sketch, "E103.MirrorCS", {"start": v(-20, -20.71) * mm, "end": v(-22, -20.71) * mm});
            skLineSegment(sketch, "E104.MirrorCS", {"start": v(-9.82, 59.99) * mm, "end": v(-11.5, 59.17) * mm});
            skLineSegment(sketch, "E105.MirrorCS", {"start": v(-20, -3.71) * mm, "end": v(-22, -3.71) * mm});
            skLineSegment(sketch, "E106.MirrorCS", {"start": v(-9.82, -8.03) * mm, "end": v(-11.56, -8.03) * mm});
            skLineSegment(sketch, "E107.MirrorCS", {"start": v(-20, 0) * mm, "end": v(-22, 0) * mm});
            skLineSegment(sketch, "E108.MirrorCS", {"start": v(-16.82, 25.97) * mm, "end": v(-18.56, 25.97) * mm});
            skLineSegment(sketch, "E109.MirrorCS", {"start": v(-16.82, -8.03) * mm, "end": v(-18.56, -8.03) * mm});
            skLineSegment(sketch, "E110.MirrorCS", {"start": v(-13, 47.29) * mm, "end": v(-15, 47.29) * mm});
            skLineSegment(sketch, "E111.MirrorCS", {"start": v(-9.82, 25.97) * mm, "end": v(-11.56, 25.97) * mm});
            skLineSegment(sketch, "E112.MirrorCS", {"start": v(-6, 68) * mm, "end": v(-8, 68) * mm});
            skLineSegment(sketch, "E113.MirrorCS", {"start": v(-23.82, -8.03) * mm, "end": v(-25.56, -8.03) * mm});
            skLineSegment(sketch, "E114.MirrorCS", {"start": v(-2.82, 6.97) * mm, "end": v(-4.56, 6.97) * mm});
            skLineSegment(sketch, "E115.MirrorCS", {"start": v(1, -17) * mm, "end": v(-1, -17) * mm});
            skLineSegment(sketch, "E116.MirrorCS", {"start": v(-9.82, 6.97) * mm, "end": v(-11.56, 6.97) * mm});
            skLineSegment(sketch, "E117.MirrorCS", {"start": v(-2.82, -25.03) * mm, "end": v(-4.56, -25.03) * mm});
            skLineSegment(sketch, "E118.MirrorCS", {"start": v(-2.82, -10.03) * mm, "end": v(-4.56, -10.03) * mm});
            skLineSegment(sketch, "E119.MirrorCS", {"start": v(1, 98.29) * mm, "end": v(-1, 98.29) * mm});
            skLineSegment(sketch, "E120.MirrorCS", {"start": v(-6, 81.29) * mm, "end": v(-8, 81.29) * mm});
            skLineSegment(sketch, "E121.MirrorCS", {"start": v(-9.82, 40.97) * mm, "end": v(-11.56, 40.97) * mm});
            skLineSegment(sketch, "E122.MirrorCS", {"start": v(-16.82, 6.97) * mm, "end": v(-18.56, 6.97) * mm});
            skLineSegment(sketch, "E123.MirrorCS", {"start": v(-37.82, -25.03) * mm, "end": v(-39.56, -25.03) * mm});
            skLineSegment(sketch, "E124.MirrorCS", {"start": v(-30.82, -25.03) * mm, "end": v(-32.56, -25.03) * mm});
            skLineSegment(sketch, "E125.MirrorCS", {"start": v(-37.82, -27.6) * mm, "end": v(-39.56, -27.6) * mm});
            skLineSegment(sketch, "E126.MirrorCS", {"start": v(-4.56, -27.6) * mm, "end": v(-2.82, -27.6) * mm});
            skLineSegment(sketch, "E127.MirrorCS", {"start": v(-23.82, 6.97) * mm, "end": v(-25.56, 6.97) * mm});
            skLineSegment(sketch, "E128.MirrorCS", {"start": v(-6, -34) * mm, "end": v(-8, -34) * mm});
            skLineSegment(sketch, "E129.MirrorCS", {"start": v(-2.82, 25.97) * mm, "end": v(-4.56, 25.97) * mm});
            skLineSegment(sketch, "E130.MirrorCS", {"start": v(-2.82, 59.97) * mm, "end": v(-4.56, 59.97) * mm});
            skLineSegment(sketch, "E131.MirrorCS", {"start": v(-6, 34) * mm, "end": v(-8, 34) * mm});
            skLineSegment(sketch, "E132.MirrorCS", {"start": v(-9.82, 42.97) * mm, "end": v(-11.56, 42.97) * mm});
            skLineSegment(sketch, "E133.MirrorCS", {"start": v(-9.82, 8.97) * mm, "end": v(-11.56, 8.97) * mm});
            skLineSegment(sketch, "E134.MirrorCS", {"start": v(-9.82, -25.03) * mm, "end": v(-11.56, -25.03) * mm});
            skLineSegment(sketch, "E135.MirrorCS", {"start": v(-16.82, 8.97) * mm, "end": v(-18.56, 8.97) * mm});
            skLineSegment(sketch, "E136.MirrorCS", {"start": v(-16.82, -25.03) * mm, "end": v(-18.56, -25.03) * mm});
            skLineSegment(sketch, "E137.MirrorCS", {"start": v(-9.82, 23.97) * mm, "end": v(-11.56, 23.97) * mm});
            skLineSegment(sketch, "E138.MirrorCS", {"start": v(-27, 0) * mm, "end": v(-29, 0) * mm});
            skLineSegment(sketch, "E139.MirrorCS", {"start": v(-16.82, 23.97) * mm, "end": v(-18.56, 23.97) * mm});
            skLineSegment(sketch, "E140.MirrorCS", {"start": v(1, -20.71) * mm, "end": v(-1, -20.71) * mm});
            skLineSegment(sketch, "E141.MirrorCS", {"start": v(-16.82, -10.03) * mm, "end": v(-18.56, -10.03) * mm});
            skLineSegment(sketch, "E142.MirrorCS", {"start": v(-23.82, -27.6) * mm, "end": v(-25.56, -27.6) * mm});
            skLineSegment(sketch, "E143.MirrorCS", {"start": v(-1, 100.63) * mm, "end": v(1, 100.63) * mm});
            skLineSegment(sketch, "E144.MirrorCS", {"start": v(-30.82, -8.03) * mm, "end": v(-32.56, -8.03) * mm});
            skLineSegment(sketch, "E145.MirrorCS", {"start": v(-1, 104.34) * mm, "end": v(1, 104.34) * mm});
            skLineSegment(sketch, "E146.MirrorCS", {"start": v(-2.82, 94.32) * mm, "end": v(-4.56, 94.32) * mm});
            skLineSegment(sketch, "E147.MirrorCS", {"start": v(-2.82, 76.97) * mm, "end": v(-4.56, 76.97) * mm});
            skLineSegment(sketch, "E148.MirrorCS", {"start": v(-37.82, -35.03) * mm, "end": v(-39.56, -35.03) * mm});
            skLineSegment(sketch, "E149.MirrorCS", {"start": v(-13, -34) * mm, "end": v(-15, -34) * mm});
            skLineSegment(sketch, "E150.MirrorCS", {"start": v(-2.82, 91.97) * mm, "end": v(-4.56, 91.97) * mm});
            skLineSegment(sketch, "E151.MirrorCS", {"start": v(-27, -34) * mm, "end": v(-29, -34) * mm});
            skLineSegment(sketch, "E152.MirrorCS", {"start": v(-34, -7.06) * mm, "end": v(-36, -17) * mm});
            skLineSegment(sketch, "E153.MirrorCS", {"start": v(-34, -34) * mm, "end": v(-36, -34) * mm});
            skLineSegment(sketch, "E154.MirrorCS", {"start": v(-32.56, -39.31) * mm, "end": v(-30.82, -39.31) * mm});
            skLineSegment(sketch, "E155.MirrorCS", {"start": v(-9.82, -35.66) * mm, "end": v(-11.56, -35.66) * mm});
            skLineSegment(sketch, "E156.MirrorCS", {"start": v(-20, -34) * mm, "end": v(-22, -34) * mm});
            skLineSegment(sketch, "E157.MirrorCS", {"start": v(-2.82, 94.32) * mm, "end": v(-2.82, 104.34) * mm});
            skLineSegment(sketch, "E158.MirrorCS", {"start": v(-2.82, 104.34) * mm, "end": v(-4.56, 104.34) * mm});
            skLineSegment(sketch, "E159.MirrorCS", {"start": v(1, 85) * mm, "end": v(-1, 85) * mm});
            skLineSegment(sketch, "E160.MirrorCS", {"start": v(1, 51) * mm, "end": v(-1, 51) * mm});
            skLineSegment(sketch, "E161.MirrorCS", {"start": v(1, 17) * mm, "end": v(-1, 17) * mm});
            skLineSegment(sketch, "E162.MirrorCS", {"start": v(1, 64.29) * mm, "end": v(-1, 64.29) * mm});
            skLineSegment(sketch, "E163.MirrorCS", {"start": v(1, 30.29) * mm, "end": v(-1, 30.29) * mm});
            skLineSegment(sketch, "E164.MirrorCS", {"start": v(1, -3.71) * mm, "end": v(-1, -3.71) * mm});
            skLineSegment(sketch, "E165.MirrorCS", {"start": v(1, 81.29) * mm, "end": v(-1, 81.29) * mm});
            skLineSegment(sketch, "E166.MirrorCS", {"start": v(-16.82, -36.37) * mm, "end": v(-18.56, -36.37) * mm});
            skLineSegment(sketch, "E167.MirrorCS", {"start": v(1, 68) * mm, "end": v(-1, 68) * mm});
            skLineSegment(sketch, "E168.MirrorCS", {"start": v(1, 0) * mm, "end": v(-1, 0) * mm});
            skLineSegment(sketch, "E169.MirrorCS", {"start": v(1, 34) * mm, "end": v(-1, 34) * mm});
            skLineSegment(sketch, "E170.MirrorCS", {"start": v(1, 47.29) * mm, "end": v(-1, 47.29) * mm});
            skLineSegment(sketch, "E171.MirrorCS", {"start": v(1, 13.29) * mm, "end": v(-1, 13.29) * mm});
            skLineSegment(sketch, "E172.MirrorCS", {"start": v(-23.82, 16.33) * mm, "end": v(-25.56, 8.97) * mm});
            skLineSegment(sketch, "E173.MirrorCS", {"start": v(-23.82, -37.43) * mm, "end": v(-25.56, -37.43) * mm});
            skLineSegment(sketch, "E174.MirrorCS", {"start": v(-13, 50.47) * mm, "end": v(-13, 57.3) * mm});
            skPoint(sketch, "E175.MirrorP", {"position": v(-14, 40.64) * mm});
            skLineSegment(sketch, "E176.MirrorCS", {"start": v(-9.82, 42.97) * mm, "end": v(-9.82, 57.97) * mm});
            skPoint(sketch, "E177.MirrorP", {"position": v(-10.7, 50.47) * mm});
            skLineSegment(sketch, "E178.MirrorCS", {"start": v(-9.82, 8.97) * mm, "end": v(-9.82, 23.97) * mm});
            skLineSegment(sketch, "E179.MirrorCS", {"start": v(-9.82, -25.03) * mm, "end": v(-9.82, -10.03) * mm});
            skLineSegment(sketch, "E180.MirrorCS", {"start": v(-16.82, 8.97) * mm, "end": v(-16.82, 23.97) * mm});
            skPoint(sketch, "E181.MirrorP", {"position": v(-21, 6.64) * mm});
            skLineSegment(sketch, "E182.MirrorCS", {"start": v(-16.82, -25.03) * mm, "end": v(-16.82, -10.03) * mm});
            skLineSegment(sketch, "E183.MirrorCS", {"start": v(-15, 34) * mm, "end": v(-15, 47.29) * mm});
            skLineSegment(sketch, "E184.MirrorCS", {"start": v(-25.56, -8.03) * mm, "end": v(-25.56, 6.97) * mm});
            skLineSegment(sketch, "E185.MirrorCS", {"start": v(-6, 0) * mm, "end": v(-6, 13.29) * mm});
            skPoint(sketch, "E186.MirrorP", {"position": v(-7, 57.64) * mm});
            skLineSegment(sketch, "E187.MirrorCS", {"start": v(-11.56, 42.97) * mm, "end": v(-11.56, 57.97) * mm});
            skLineSegment(sketch, "E188.MirrorCS", {"start": v(-11.56, 8.97) * mm, "end": v(-11.56, 23.97) * mm});
            skLineSegment(sketch, "E189.MirrorCS", {"start": v(-11.56, -25.03) * mm, "end": v(-11.56, -10.03) * mm});
            skLineSegment(sketch, "E190.MirrorCS", {"start": v(-37.82, -25.03) * mm, "end": v(-37.82, -17) * mm});
            skPoint(sketch, "E191.MirrorP", {"position": v(-3.7, 50.47) * mm});
            skPoint(sketch, "E192.MirrorP", {"position": v(-3.7, -0.53) * mm});
            skLineSegment(sketch, "E193.MirrorCS", {"start": v(-18.56, 8.97) * mm, "end": v(-18.56, 23.97) * mm});
            skPoint(sketch, "E194.MirrorP", {"position": v(-28, -27.36) * mm});
            skLineSegment(sketch, "E195.MirrorCS", {"start": v(-23.82, -27.6) * mm, "end": v(-23.82, -37.43) * mm});
            skLineSegment(sketch, "E196.MirrorCS", {"start": v(-18.56, -25.03) * mm, "end": v(-18.56, -10.03) * mm});
            skLineSegment(sketch, "E197.MirrorCS", {"start": v(-27, 9.49) * mm, "end": v(-29, 0) * mm});
            skLineSegment(sketch, "E198.MirrorCS", {"start": v(-13, -34) * mm, "end": v(-13, -20.71) * mm});
            skLineSegment(sketch, "E199.MirrorCS", {"start": v(-9.82, 25.97) * mm, "end": v(-9.82, 40.97) * mm});
            skPoint(sketch, "E200.MirrorP", {"position": v(-7, 74.64) * mm});
            skPoint(sketch, "E201.MirrorP", {"position": v(-7, 6.64) * mm});
            skLineSegment(sketch, "E202.MirrorCS", {"start": v(-20, 17) * mm, "end": v(-20, 30.29) * mm});
            skLineSegment(sketch, "E203.MirrorCS", {"start": v(-23.82, -25.03) * mm, "end": v(-23.82, -10.03) * mm});
            skPoint(sketch, "E204.MirrorP", {"position": v(-10.7, -17.53) * mm});
            skPoint(sketch, "E205.MirrorP", {"position": v(-31.7, -17.53) * mm});
            skLineSegment(sketch, "E206.MirrorCS", {"start": v(-25.56, -27.6) * mm, "end": v(-25.56, -37.43) * mm});
            skLineSegment(sketch, "E207.MirrorCS", {"start": v(-27, 0) * mm, "end": v(-27, 9.49) * mm});
            skLineSegment(sketch, "E208.MirrorCS", {"start": v(-30.61, 2.6) * mm, "end": v(-32.56, -8.03) * mm});
            skLineSegment(sketch, "E209.MirrorCS", {"start": v(-6, 68) * mm, "end": v(-6, 81.29) * mm});
            skLineSegment(sketch, "E210.MirrorCS", {"start": v(-13, 34) * mm, "end": v(-13, 47.29) * mm});
            skLineSegment(sketch, "E211.MirrorCS", {"start": v(-2.82, 59.97) * mm, "end": v(-2.82, 74.97) * mm});
            skLineSegment(sketch, "E212.MirrorCS", {"start": v(-13, 57.3) * mm, "end": v(-14.36, 49.35) * mm});
            skPoint(sketch, "E213.MirrorP", {"position": v(-14, -27.36) * mm});
            skPoint(sketch, "E214.MirrorP", {"position": v(-3.7, 67.47) * mm});
            skLineSegment(sketch, "E215.MirrorCS", {"start": v(-25.56, -25.03) * mm, "end": v(-25.56, -10.03) * mm});
            skPoint(sketch, "E216.MirrorP", {"position": v(-28, -10.36) * mm});
            skLineSegment(sketch, "E217.MirrorCS", {"start": v(-18.56, -8.03) * mm, "end": v(-18.56, 6.97) * mm});
            skLineSegment(sketch, "E218.MirrorCS", {"start": v(-32.56, -25.03) * mm, "end": v(-32.56, -10.03) * mm});
            skLineSegment(sketch, "E219.MirrorCS", {"start": v(-16.82, -8.03) * mm, "end": v(-16.82, 6.97) * mm});
            skPoint(sketch, "E220.MirrorP", {"position": v(-17.7, 16.47) * mm});
            skPoint(sketch, "E221.MirrorP", {"position": v(-3.7, 16.47) * mm});
            skLineSegment(sketch, "E222.MirrorCS", {"start": v(-2.82, 42.97) * mm, "end": v(-2.82, 57.97) * mm});
            skLineSegment(sketch, "E223.MirrorCS", {"start": v(-2.82, 8.97) * mm, "end": v(-2.82, 23.97) * mm});
            skLineSegment(sketch, "E224.MirrorCS", {"start": v(-6, 51) * mm, "end": v(-6, 64.29) * mm});
            skPoint(sketch, "E225.MirrorP", {"position": v(-17.7, -17.53) * mm});
            skLineSegment(sketch, "E226.MirrorCS", {"start": v(-6, 17) * mm, "end": v(-6, 30.29) * mm});
            skLineSegment(sketch, "E227.MirrorCS", {"start": v(-6, -17) * mm, "end": v(-6, -3.71) * mm});
            skLineSegment(sketch, "E228.MirrorCS", {"start": v(-2.82, 76.97) * mm, "end": v(-2.82, 91.97) * mm});
            skLineSegment(sketch, "E229.MirrorCS", {"start": v(-8, 0) * mm, "end": v(-8, 13.29) * mm});
            skLineSegment(sketch, "E230.MirrorCS", {"start": v(-8, -34) * mm, "end": v(-8, -20.71) * mm});
            skPoint(sketch, "E231.MirrorP", {"position": v(-35, -27.36) * mm});
            skLineSegment(sketch, "E232.MirrorCS", {"start": v(-13, 17) * mm, "end": v(-13, 30.29) * mm});
            skLineSegment(sketch, "E233.MirrorCS", {"start": v(-13, -17) * mm, "end": v(-13, -3.71) * mm});
            skLineSegment(sketch, "E234.MirrorCS", {"start": v(-37.82, -17) * mm, "end": v(-39.56, -25.03) * mm});
            skLineSegment(sketch, "E235.MirrorCS", {"start": v(-4.56, 59.97) * mm, "end": v(-4.56, 74.97) * mm});
            skLineSegment(sketch, "E236.MirrorCS", {"start": v(-8, -17) * mm, "end": v(-8, -3.71) * mm});
            skLineSegment(sketch, "E237.MirrorCS", {"start": v(-4.56, 76.97) * mm, "end": v(-4.56, 91.97) * mm});
            skLineSegment(sketch, "E238.MirrorCS", {"start": v(-4.56, 42.97) * mm, "end": v(-4.56, 57.97) * mm});
            skLineSegment(sketch, "E239.MirrorCS", {"start": v(-4.56, 8.97) * mm, "end": v(-4.56, 23.97) * mm});
            skLineSegment(sketch, "E240.MirrorCS", {"start": v(-15, 0) * mm, "end": v(-15, 13.29) * mm});
            skLineSegment(sketch, "E241.MirrorCS", {"start": v(-15, -34) * mm, "end": v(-15, -20.71) * mm});
            skLineSegment(sketch, "E242.MirrorCS", {"start": v(-15, 17) * mm, "end": v(-15, 30.29) * mm});
            skLineSegment(sketch, "E243.MirrorCS", {"start": v(-15, -17) * mm, "end": v(-15, -3.71) * mm});
            skPoint(sketch, "E244.MirrorP", {"position": v(-10.72, 65.76) * mm});
            skPoint(sketch, "E245.MirrorP", {"position": v(-24.7, -17.53) * mm});
            skPoint(sketch, "E246.MirrorP", {"position": v(-14, -10.36) * mm});
            skLineSegment(sketch, "E247.MirrorCS", {"start": v(-16.82, -27.6) * mm, "end": v(-16.82, -36.37) * mm});
            skLineSegment(sketch, "E248.MirrorCS", {"start": v(-8, 51) * mm, "end": v(-8, 64.29) * mm});
            skPoint(sketch, "E249.MirrorP", {"position": v(-3.7, 84.47) * mm});
            skLineSegment(sketch, "E250.MirrorCS", {"start": v(-8, 17) * mm, "end": v(-8, 30.29) * mm});
            skLineSegment(sketch, "E251.MirrorCS", {"start": v(-27, -34) * mm, "end": v(-27, -20.71) * mm});
            skLineSegment(sketch, "E252.MirrorCS", {"start": v(-34, -34) * mm, "end": v(-34, -20.71) * mm});
            skLineSegment(sketch, "E253.MirrorCS", {"start": v(-32.56, -27.6) * mm, "end": v(-32.56, -39.31) * mm});
            skLineSegment(sketch, "E254.MirrorCS", {"start": v(-9.82, -27.6) * mm, "end": v(-9.82, -35.66) * mm});
            skPoint(sketch, "E255.MirrorP", {"position": v(-14, 23.64) * mm});
            skLineSegment(sketch, "E256.MirrorCS", {"start": v(-16.82, 40.97) * mm, "end": v(-18.56, 25.97) * mm});
            skPoint(sketch, "E257.MirrorP", {"position": v(-17.7, -0.53) * mm});
            skLineSegment(sketch, "E258.MirrorCS", {"start": v(-8, 68) * mm, "end": v(-8, 81.29) * mm});
            skLineSegment(sketch, "E259.MirrorCS", {"start": v(-20, -17) * mm, "end": v(-20, -3.71) * mm});
            skLineSegment(sketch, "E260.MirrorCS", {"start": v(-23.82, -8.03) * mm, "end": v(-23.82, 6.97) * mm});
            skLineSegment(sketch, "E261.MirrorCS", {"start": v(-11.56, -27.6) * mm, "end": v(-11.56, -35.66) * mm});
            skLineSegment(sketch, "E262.MirrorCS", {"start": v(-27, -17) * mm, "end": v(-27, -3.71) * mm});
            skLineSegment(sketch, "E263.MirrorCS", {"start": v(-39.56, -27.6) * mm, "end": v(-39.56, -35.03) * mm});
            skPoint(sketch, "E264.MirrorP", {"position": v(-3.7, -17.53) * mm});
            skLineSegment(sketch, "E265.MirrorCS", {"start": v(-2.82, -27.6) * mm, "end": v(-2.82, -34) * mm});
            skLineSegment(sketch, "E266.MirrorCS", {"start": v(1, -34) * mm, "end": v(1, -17) * mm, "construction": true});
            skPoint(sketch, "E267.MirrorP", {"position": v(-7, -10.36) * mm});
            skLineSegment(sketch, "E268.MirrorCS", {"start": v(-2.82, -25.03) * mm, "end": v(-2.82, -10.03) * mm});
            skLineSegment(sketch, "E269.MirrorCS", {"start": v(-16.82, 25.97) * mm, "end": v(-16.82, 40.97) * mm});
            skPoint(sketch, "E270.MirrorP", {"position": v(-14, 6.64) * mm});
            skPoint(sketch, "E271.MirrorP", {"position": v(-7, -27.36) * mm});
            skLineSegment(sketch, "E272.MirrorCS", {"start": v(-9.72, 73.26) * mm, "end": v(-11.5, 59.17) * mm});
            skLineSegment(sketch, "E273.MirrorCS", {"start": v(-22, -17) * mm, "end": v(-22, -3.71) * mm});
            skLineSegment(sketch, "E274.MirrorCS", {"start": v(-29, -17) * mm, "end": v(-29, -3.71) * mm});
            skLineSegment(sketch, "E275.MirrorCS", {"start": v(-11.56, 25.97) * mm, "end": v(-11.56, 40.97) * mm});
            skLineSegment(sketch, "E276.MirrorCS", {"start": v(-11.56, -8.03) * mm, "end": v(-11.56, 6.97) * mm});
            skLineSegment(sketch, "E277.MirrorCS", {"start": v(-30.82, -25.03) * mm, "end": v(-30.82, -10.03) * mm});
            skLineSegment(sketch, "E278.MirrorCS", {"start": v(-2.82, 25.97) * mm, "end": v(-2.82, 40.97) * mm});
            skLineSegment(sketch, "E279.MirrorCS", {"start": v(-37.82, -27.6) * mm, "end": v(-37.82, -35.03) * mm});
            skPoint(sketch, "E280.MirrorP", {"position": v(-10.7, 16.47) * mm});
            skLineSegment(sketch, "E281.MirrorCS", {"start": v(-6, 34) * mm, "end": v(-6, 47.29) * mm});
            skLineSegment(sketch, "E282.MirrorCS", {"start": v(-9.82, -8.03) * mm, "end": v(-9.82, 6.97) * mm});
            skLineSegment(sketch, "E283.MirrorCS", {"start": v(-6, -34) * mm, "end": v(-6, -20.71) * mm});
            skPoint(sketch, "E284.MirrorP", {"position": v(-21, -27.36) * mm});
            skPoint(sketch, "E285.MirrorP", {"position": v(-17.7, 33.47) * mm});
            skPoint(sketch, "E286.MirrorP", {"position": v(-10.7, -0.53) * mm});
            skLineSegment(sketch, "E287.MirrorCS", {"start": v(-34, -17) * mm, "end": v(-34, -7.06) * mm});
            skLineSegment(sketch, "E288.MirrorCS", {"start": v(-4.56, 25.97) * mm, "end": v(-4.56, 40.97) * mm});
            skLineSegment(sketch, "E289.MirrorCS", {"start": v(-4.56, -25.03) * mm, "end": v(-4.56, -10.03) * mm});
            skPoint(sketch, "E290.MirrorP", {"position": v(-7, 23.64) * mm});
            skLineSegment(sketch, "E291.MirrorCS", {"start": v(-8, 34) * mm, "end": v(-8, 47.29) * mm});
            skPoint(sketch, "E292.MirrorP", {"position": v(-10.7, 33.47) * mm});
            skLineSegment(sketch, "E293.MirrorCS", {"start": v(-13, 0) * mm, "end": v(-13, 13.29) * mm});
            skLineSegment(sketch, "E294.MirrorCS", {"start": v(-20, 0) * mm, "end": v(-20, 13.29) * mm});
            skLineSegment(sketch, "E295.MirrorCS", {"start": v(-20, -34) * mm, "end": v(-20, -20.71) * mm});
            skPoint(sketch, "E296.MirrorP", {"position": v(-21, -10.36) * mm});
            skLineSegment(sketch, "E297.MirrorCS", {"start": v(-18.56, -27.6) * mm, "end": v(-18.56, -36.37) * mm});
            skLineSegment(sketch, "E298.MirrorCS", {"start": v(-4.56, 94.32) * mm, "end": v(-4.56, 104.34) * mm});
            skLineSegment(sketch, "E299.MirrorCS", {"start": v(-20, 30.29) * mm, "end": v(-22, 17) * mm});
            skLineSegment(sketch, "E300.MirrorCS", {"start": v(-4.56, -27.6) * mm, "end": v(-4.56, -34) * mm});
            skLineSegment(sketch, "E301.MirrorCS", {"start": v(-22, 0) * mm, "end": v(-22, 13.29) * mm});
            skLineSegment(sketch, "E302.MirrorCS", {"start": v(-22, -34) * mm, "end": v(-22, -20.71) * mm});
            skPoint(sketch, "E303.MirrorP", {"position": v(-7, 40.64) * mm});
            skPoint(sketch, "E304.MirrorP", {"position": v(-3.7, 33.47) * mm});
            skPoint(sketch, "E305.MirrorP", {"position": v(-14, 56.26) * mm});
            skLineSegment(sketch, "E306.MirrorCS", {"start": v(-9.82, 59.99) * mm, "end": v(-9.72, 73.26) * mm});
            skLineSegment(sketch, "E307.MirrorCS", {"start": v(-29, -34) * mm, "end": v(-29, -20.71) * mm});
            skLineSegment(sketch, "E308.MirrorCS", {"start": v(-36, -34) * mm, "end": v(-36, -20.71) * mm});
            skLineSegment(sketch, "E309.MirrorCS", {"start": v(-2.82, -8.03) * mm, "end": v(-2.82, 6.97) * mm});
            skLineSegment(sketch, "E310.MirrorCS", {"start": v(-4.56, -8.03) * mm, "end": v(-4.56, 6.97) * mm});
            skLineSegment(sketch, "E311.MirrorCS", {"start": v(-30.82, -27.6) * mm, "end": v(-30.82, -39.31) * mm});
            skPoint(sketch, "E312.MirrorP", {"position": v(-24.7, -0.53) * mm});
            skLineSegment(sketch, "E313.MirrorCS", {"start": v(-23.82, 8.97) * mm, "end": v(-23.82, 16.33) * mm});
            skLineSegment(sketch, "E314.MirrorCS", {"start": v(-30.82, -8.03) * mm, "end": v(-30.82, 1.15) * mm});
            skSolve(sketch);
        }
        {
            var Q0;
            Q0 = qSketchRegion(id + "F2", true);
            extrude(context, id + "F3", {"entities" : qUnion([Q0]), "operationType" : NewBodyOperationType.REMOVE, "oppositeDirection" : true, "depth" : 3 * mm});
        }
    });
